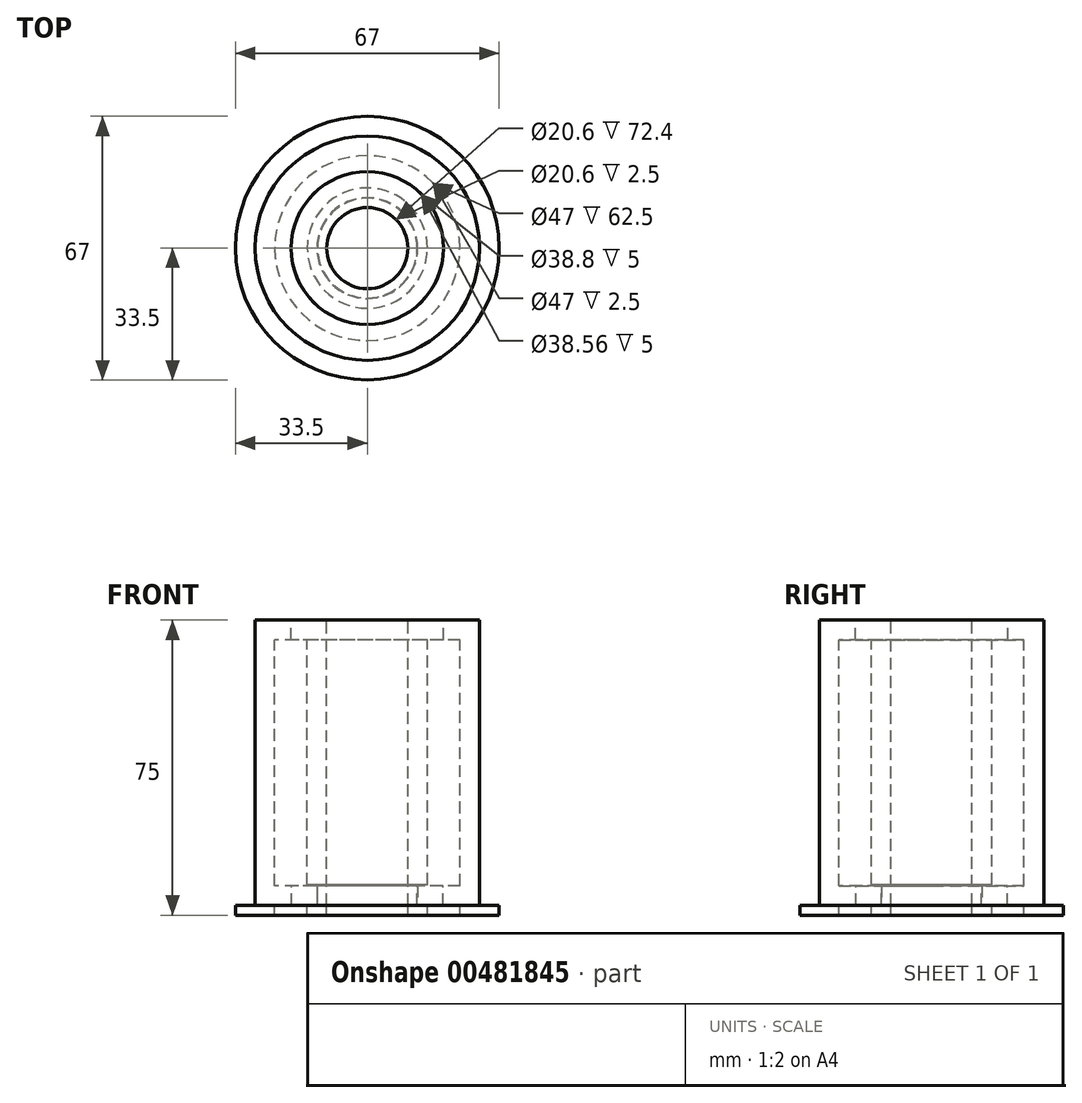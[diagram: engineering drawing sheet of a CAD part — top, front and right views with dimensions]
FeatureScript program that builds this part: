
annotation { "Feature Type Name" : "Feature", "Feature Type Description" : "" }
export const myFeature = defineFeature(function(context is Context, id is Id, definition is map)
    precondition{}
    {
        {
            var Q0;
            Q0=qCreatedBy(makeId("Front.planeOp"),FACE);
            var sketch = newSketch(context, id + "F0", { "sketchPlane" : qUnion([Q0])});
            skLineSegment(sketch, "E0", {"start": v(0, 49.2) * mm, "end": v(0, -47.14) * mm, "construction": true});
            skLineSegment(sketch, "E1.left", {"start": v(-10.3, 41.28) * mm, "end": v(-10.3, -26.12) * mm});
            skLineSegment(sketch, "E2", {"start": v(-15.28, -21.22) * mm, "end": v(-12.78, -21.22) * mm});
            skLineSegment(sketch, "E3", {"start": v(-10.3, -26.22) * mm, "end": v(-12.8, -26.22) * mm});
            skLineSegment(sketch, "E4", {"start": v(-12.8, -26.22) * mm, "end": v(-12.78, -21.22) * mm});
            skLineSegment(sketch, "E5", {"start": v(-10.3, 41.28) * mm, "end": v(-10.3, 46.28) * mm});
            skLineSegment(sketch, "E6", {"start": v(-15.28, -20.95) * mm, "end": v(-15.28, 41.28) * mm});
            skLineSegment(sketch, "E7", {"start": v(-15.28, 41.28) * mm, "end": v(-19.4, 41.28) * mm, "construction": true});
            skLineSegment(sketch, "E8", {"start": v(-23.5, 41.28) * mm, "end": v(-23.5, -21.22) * mm});
            skLineSegment(sketch, "E9", {"start": v(0, 0) * mm, "end": v(-47.71, 0) * mm, "construction": true});
            skPoint(sketch, "E10", {"position": v(-19.4, 41.28) * mm});
            skLineSegment(sketch, "E11.bottom", {"start": v(-10.3, 46.28) * mm, "end": v(-19.4, 46.28) * mm});
            skLineSegment(sketch, "E11.top", {"start": v(-15.28, 41.28) * mm, "end": v(-19.4, 41.28) * mm});
            skLineSegment(sketch, "E11.left", {"start": v(-10.3, 46.28) * mm, "end": v(-10.3, 41.28) * mm});
            skLineSegment(sketch, "E11.right", {"start": v(-19.4, 46.28) * mm, "end": v(-19.4, 41.28) * mm});
            skLineSegment(sketch, "E12.right", {"start": v(-28.5, 41.28) * mm, "end": v(-28.5, -26.22) * mm});
            skLineSegment(sketch, "E13.bottom", {"start": v(-23.5, 41.28) * mm, "end": v(-19.4, 41.28) * mm});
            skLineSegment(sketch, "E13.top", {"start": v(-28.5, 46.28) * mm, "end": v(-19.4, 46.28) * mm});
            skLineSegment(sketch, "E13.left", {"start": v(-28.5, 41.28) * mm, "end": v(-28.5, 46.28) * mm});
            skLineSegment(sketch, "E13.right", {"start": v(-19.4, 41.28) * mm, "end": v(-19.4, 46.28) * mm});
            skLineSegment(sketch, "E14.bottom", {"start": v(-23.5, -26.22) * mm, "end": v(-19.28, -26.22) * mm});
            skLineSegment(sketch, "E14.top", {"start": v(-23.5, -21.22) * mm, "end": v(-19.28, -21.22) * mm});
            skLineSegment(sketch, "E15.bottom", {"start": v(-12.8, -26.22) * mm, "end": v(-12.55, -26.22) * mm});
            skLineSegment(sketch, "E15.top", {"start": v(-15.28, -28.72) * mm, "end": v(-10.3, -28.72) * mm});
            skLineSegment(sketch, "E15.left", {"start": v(-15.28, -26.22) * mm, "end": v(-15.28, -28.72) * mm});
            skLineSegment(sketch, "E15.right", {"start": v(-10.3, -26.22) * mm, "end": v(-10.3, -28.72) * mm});
            skLineSegment(sketch, "E16", {"start": v(-19.27, -21.22) * mm, "end": v(-19.27, -26.22) * mm});
            skLineSegment(sketch, "E17.right", {"start": v(-19.28, -21.22) * mm, "end": v(-19.28, -26.22) * mm});
            skLineSegment(sketch, "E18.top", {"start": v(-15.28, -20.95) * mm, "end": v(-12.78, -20.95) * mm});
            skLineSegment(sketch, "E19.bottom", {"start": v(-12.78, -20.95) * mm, "end": v(-12.68, -20.95) * mm});
            skLineSegment(sketch, "E19.right", {"start": v(-12.68, -20.95) * mm, "end": v(-12.68, -26.12) * mm});
            skLineSegment(sketch, "E20.bottom", {"start": v(-12.68, -26.22) * mm, "end": v(-10.07, -26.22) * mm});
            skLineSegment(sketch, "E20.top", {"start": v(-12.68, -26.12) * mm, "end": v(-10.3, -26.12) * mm});
            skLineSegment(sketch, "E21.trimOffspring", {"start": v(-12.68, -26.22) * mm, "end": v(-10.3, -26.22) * mm});
            skLineSegment(sketch, "E22.trimOffspring", {"start": v(-19.4, 41.28) * mm, "end": v(-23.5, 41.28) * mm, "construction": true});
            skLineSegment(sketch, "E23.trimOffspring", {"start": v(-19.27, -21.22) * mm, "end": v(-12.78, -21.22) * mm});
            skLineSegment(sketch, "E24.trimOffspring", {"start": v(-19.27, -26.22) * mm, "end": v(-15.28, -26.22) * mm});
            skLineSegment(sketch, "E25.bottom", {"start": v(-28.5, -26.22) * mm, "end": v(-33.5, -26.22) * mm});
            skLineSegment(sketch, "E25.top", {"start": v(-23.5, -28.72) * mm, "end": v(-33.5, -28.72) * mm});
            skLineSegment(sketch, "E25.left", {"start": v(-23.5, -26.22) * mm, "end": v(-23.5, -28.72) * mm});
            skLineSegment(sketch, "E25.right", {"start": v(-33.5, -26.22) * mm, "end": v(-33.5, -28.72) * mm});
            skSolve(sketch);
        }
        {
            var Q0;
            Q0=makeQuery(id+"F0.imprint","IMPRINT",FACE,{"disambiguationData":[TD([[makeQuery(id+"F0.imprint","IMPRINT",EDGE,{"derivedFrom":sQuery(id+"F0.wireOp",EDGE,"E1.left")}),-1.0]])]});
            var Q1;
            Q1=makeQuery(id+"F0.imprint","IMPRINT",FACE,{"disambiguationData":[TD([[makeQuery(id+"F0.imprint","IMPRINT",EDGE,{"derivedFrom":sQuery(id+"F0.wireOp",EDGE,"E8")}),-1.0]])]});
            var Q2;
            {var subQ2=sQuery(id+"F0.wireOp",EDGE,"E4");Q2=makeQuery(id+"F0.imprint","IMPRINT",FACE,{"disambiguationData":[TD([[makeQuery(id+"F0.imprint","IMPRINT",EDGE,{"derivedFrom":subQ2}),1.0]])]});}
            var Q3;
            Q3=sQuery(id+"F0.wireOp",EDGE,"E0");
            revolve(context, id + "F1", {"entities" : qUnion([Q0, Q1, Q2]), "axis" : qUnion([Q3]), "revolveType" : RevolveType.FULL});
        }
    });
